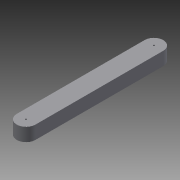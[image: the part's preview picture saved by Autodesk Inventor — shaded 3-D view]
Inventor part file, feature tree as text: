
AUTODESK INVENTOR PART (.ipt)
format: ipt  version: 2015 (Build 190159000, 159)  size: 84,480 bytes
history: native  units: in
note: dims shown in document units (in); Inventor stores cm internally (conversion verified against a paired STEP export)
features: extrude x2, sketch x2, projected_geometry x1
ambient origin geometry x8: Origin, YZ Plane, XZ Plane, XY Plane, X Axis, Y Axis, Z Axis, Center Point
bodies: Solid1 (feature_tree)
feature tree (5):
  extrude  "Extrusion1"  Depth=2.185in
  extrude  "Extrusion2"  Depth=1.555in
  sketch  "Sketch1"  dims[d0=2.185in d1=15.0in]
  sketch  "Sketch2"  dims[d2=1.555in d3=0.0in d4=0.185in d5=0.185in d6=1.555in d7=0.0in]
  projected_geometry  "Projected Loop1"
